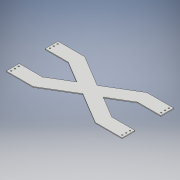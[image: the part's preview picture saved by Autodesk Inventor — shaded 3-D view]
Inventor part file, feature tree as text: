
AUTODESK INVENTOR PART (.ipt)
format: ipt  version: 2018 (Build 220112000, 112)  size: 130,048 bytes
history: native  units: mm
features: extrude x1, sketch x1, other x1
ambient origin geometry x8: Origin, YZ Plane, XZ Plane, XY Plane, X Axis, Y Axis, Z Axis, Center Point
bodies: Solid1 (feature_tree)
feature tree (3):
  extrude  "Extrusion1"  Depth=8.763mm
  sketch  "Sketch1"  dims[d0=5.1054mm d1=8.763mm d2=10.0mm d3=30.0mm d5=15.0mm d6=10.0mm d8=10.0mm d10=10.0mm d11=0.0mm]
  other  "tube frame"
